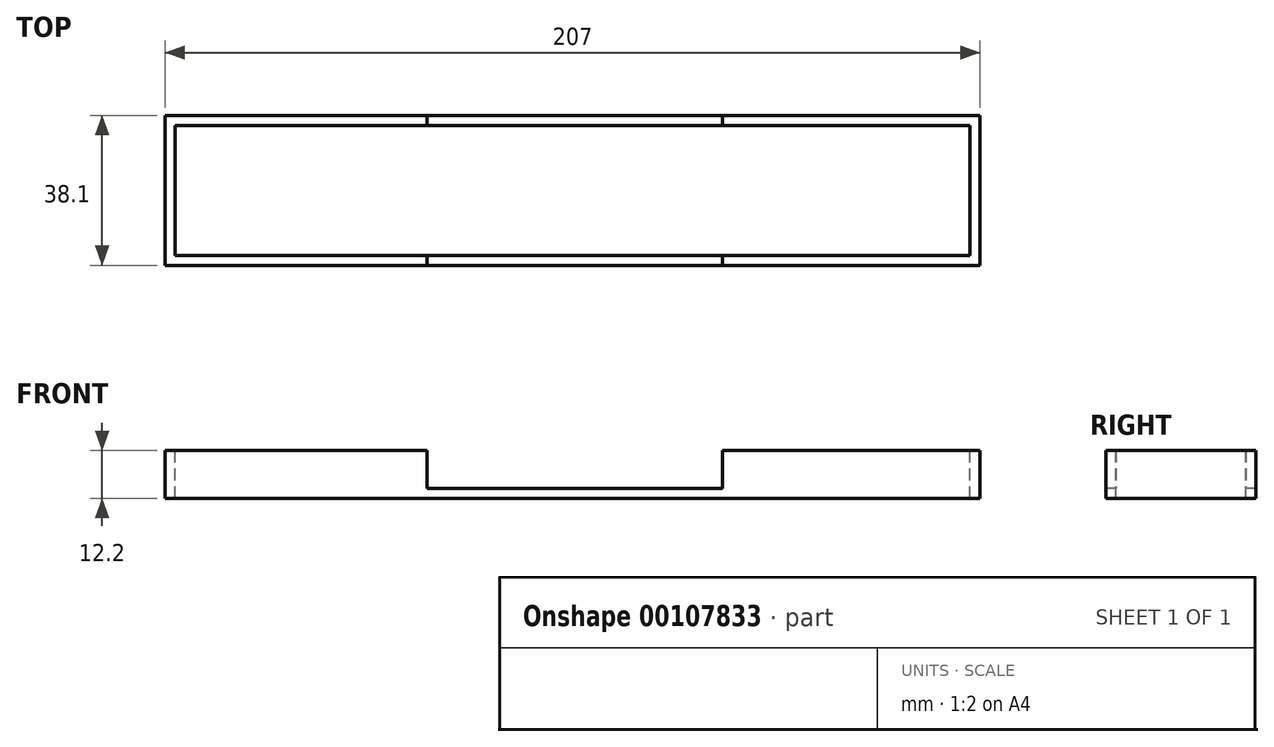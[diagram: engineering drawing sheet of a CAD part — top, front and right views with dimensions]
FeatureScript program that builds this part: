
annotation { "Feature Type Name" : "Feature", "Feature Type Description" : "" }
export const myFeature = defineFeature(function(context is Context, id is Id, definition is map)
    precondition{}
    {
        {
            var Q0;
            Q0=qCreatedBy(makeId("Front.planeOp"),FACE);
            var sketch = newSketch(context, id + "F0", { "sketchPlane" : qUnion([Q0])});
            skLineSegment(sketch, "E0.bottom", {"start": v(103.5, -6.1) * mm, "end": v(-103.5, -6.1) * mm});
            skLineSegment(sketch, "E0.left", {"start": v(103.5, -6.1) * mm, "end": v(103.5, 6.1) * mm});
            skLineSegment(sketch, "E0.right", {"start": v(-103.5, -6.1) * mm, "end": v(-103.5, 6.1) * mm});
            skPoint(sketch, "E0.middle", {"position": v(0, 0) * mm});
            skLineSegment(sketch, "E1", {"start": v(-103.5, 6.1) * mm, "end": v(-36.9, 6.1) * mm});
            skLineSegment(sketch, "E2", {"start": v(-36.9, 6.1) * mm, "end": v(-36.9, -3.56) * mm});
            skLineSegment(sketch, "E3", {"start": v(-36.9, -3.56) * mm, "end": v(38.12, -3.56) * mm});
            skLineSegment(sketch, "E4", {"start": v(38.12, -3.56) * mm, "end": v(38.12, 6.1) * mm});
            skLineSegment(sketch, "E5", {"start": v(38.12, 6.1) * mm, "end": v(103.5, 6.1) * mm});
            skSolve(sketch);
        }
        {
            var Q0;
            Q0=qSketchRegion(id+"F0",true);
            extrude(context, id + "F1", {"entities" : qUnion([Q0]), "oppositeDirection" : true, "depth" : 38.1 * mm});
        }
        {
            var Q0;
            Q0=makeQuery(id+"F1.opExtrude","SWEPT_FACE",FACE,{"disambiguationData":[OSD([sQuery(id+"F0.wireOp",EDGE,"E1")])]});
            var sketch = newSketch(context, id + "F2", { "sketchPlane" : qUnion([Q0])});
            skLineSegment(sketch, "E6.bottom", {"start": v(-100.97, 35.56) * mm, "end": v(100.97, 35.56) * mm});
            skLineSegment(sketch, "E6.top", {"start": v(-100.97, 2.54) * mm, "end": v(100.97, 2.54) * mm});
            skLineSegment(sketch, "E6.left", {"start": v(-100.97, 35.56) * mm, "end": v(-100.97, 2.54) * mm});
            skLineSegment(sketch, "E6.right", {"start": v(100.97, 35.56) * mm, "end": v(100.97, 2.54) * mm});
            skSolve(sketch);
        }
        {
            var Q0;
            Q0=qSketchRegion(id+"F2",true);
            extrude(context, id + "F3", {"entities" : qUnion([Q0]), "operationType" : NewBodyOperationType.REMOVE, "endBound" : BoundingType.THROUGH_ALL, "oppositeDirection" : true, "depth" : 9.78 * mm});
        }
    });
